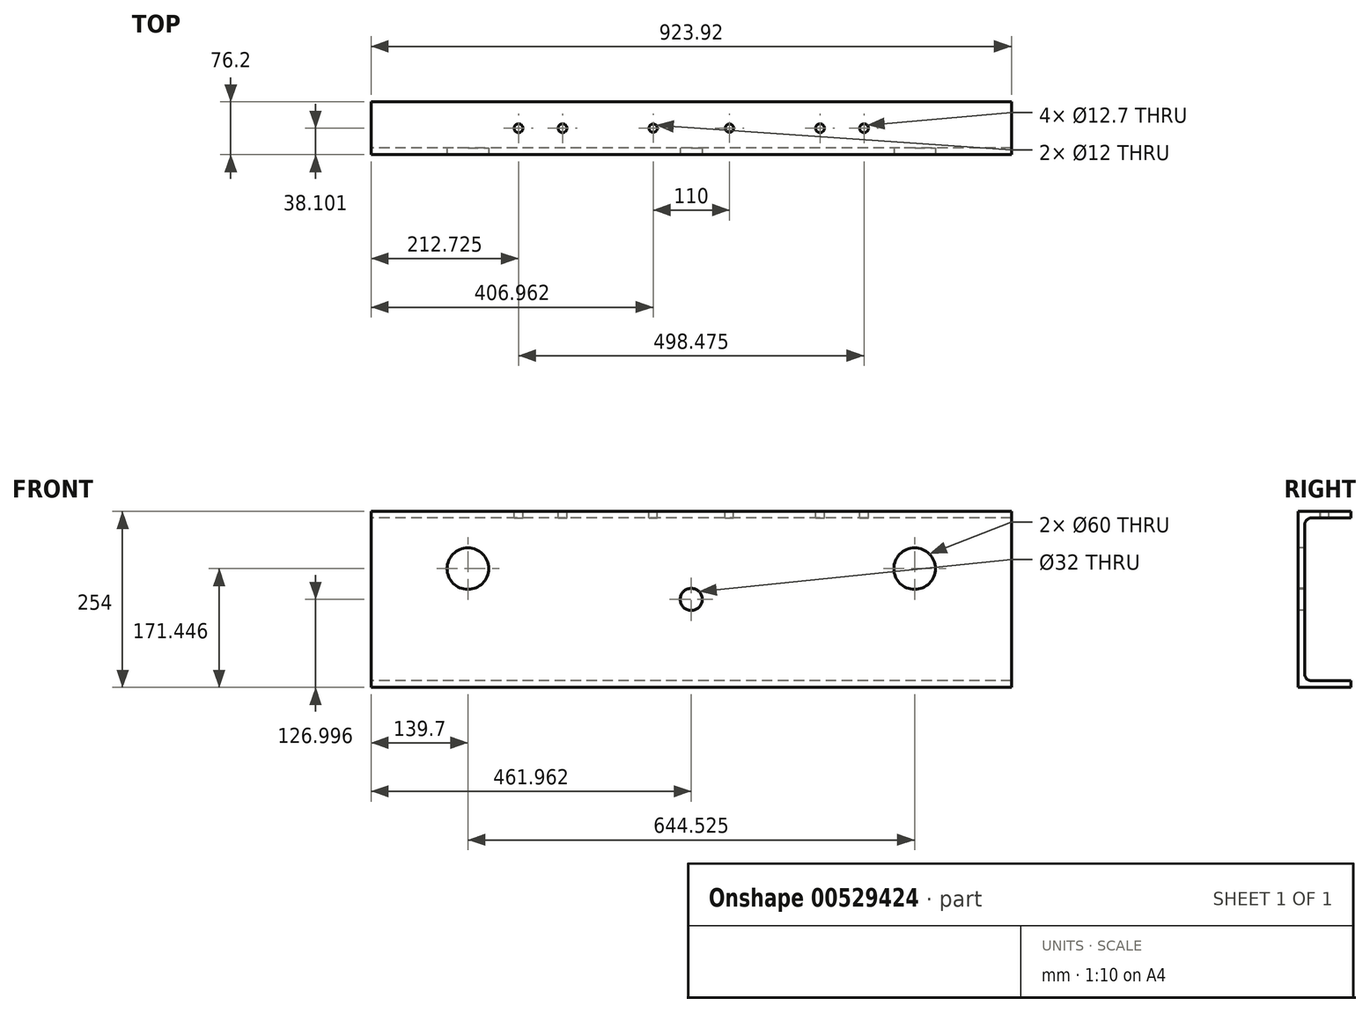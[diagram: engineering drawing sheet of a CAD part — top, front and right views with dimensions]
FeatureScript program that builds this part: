
annotation { "Feature Type Name" : "Feature", "Feature Type Description" : "" }
export const myFeature = defineFeature(function(context is Context, id is Id, definition is map)
    precondition{}
    {
        {
            var Q0;
            Q0=qCreatedBy(makeId("Right.planeOp"),FACE);
            var sketch = newSketch(context, id + "F0", { "sketchPlane" : qUnion([Q0])});
            skLineSegment(sketch, "E0", {"start": v(-26.57, -122.46) * mm, "end": v(-26.57, 131.54) * mm});
            skLineSegment(sketch, "E1", {"start": v(-26.57, 131.54) * mm, "end": v(49.63, 131.54) * mm});
            skLineSegment(sketch, "E2", {"start": v(49.63, 131.54) * mm, "end": v(49.63, 122.01) * mm});
            skLineSegment(sketch, "E3", {"start": v(49.63, 122.01) * mm, "end": v(-7.52, 122.01) * mm});
            skLineSegment(sketch, "E4", {"start": v(-17.04, 112.49) * mm, "end": v(-17.04, -103.41) * mm});
            skLineSegment(sketch, "E5", {"start": v(-7.52, -112.94) * mm, "end": v(49.63, -112.94) * mm});
            skLineSegment(sketch, "E6", {"start": v(49.63, -112.94) * mm, "end": v(49.63, -122.46) * mm});
            skLineSegment(sketch, "E7", {"start": v(49.63, -122.46) * mm, "end": v(-26.57, -122.46) * mm});
            skPoint(sketch, "E8.visualSharp", {"position": v(-17.04, 122.01) * mm});
            skArc(sketch, "E8.filletArc", {"start": v(-7.52, 122.01) * mm, "mid": v(-14.25, 119.22) * mm, "end": v(-17.04, 112.49) * mm});
            skPoint(sketch, "E9.visualSharp", {"position": v(-17.04, -112.94) * mm});
            skArc(sketch, "E9.filletArc", {"start": v(-17.04, -103.41) * mm, "mid": v(-14.25, -110.15) * mm, "end": v(-7.52, -112.94) * mm});
            skLineSegment(sketch, "E10", {"start": v(-26.57, -122.46) * mm, "end": v(-26.57, 4.54) * mm, "construction": true});
            skLineSegment(sketch, "E11", {"start": v(-26.57, 4.54) * mm, "end": v(-39.42, 4.54) * mm, "construction": true});
            skSolve(sketch);
        }
        {
            var Q0;
            Q0=makeQuery(id+"F0.imprint","IMPRINT",FACE,{"disambiguationData":[TD([[makeQuery(id+"F0.imprint","IMPRINT",EDGE,{"derivedFrom":sQuery(id+"F0.wireOp",EDGE,"E0")}),-1.0]])]});
            extrude(context, id + "F1", {"entities" : qUnion([Q0]), "depth" : 923.92 * mm, "offsetDistance" : 25 * mm});
        }
        {
            var Q0;
            Q0=makeQuery(id+"F1.opExtrude","SWEPT_FACE",FACE,{"disambiguationData":[OSD([sQuery(id+"F0.wireOp",EDGE,"E1")])]});
            var sketch = newSketch(context, id + "F2", { "sketchPlane" : qUnion([Q0])});
            skLineSegment(sketch, "E12.0", {"start": v(0, -26.57) * mm, "end": v(0, 49.63) * mm});
            skLineSegment(sketch, "E13.0", {"start": v(923.92, -26.57) * mm, "end": v(923.92, 49.63) * mm});
            skLineSegment(sketch, "E14", {"start": v(0, 11.53) * mm, "end": v(406.96, 11.53) * mm, "construction": true});
            skPoint(sketch, "E15", {"position": v(212.72, 11.53) * mm});
            skPoint(sketch, "E16", {"position": v(647.7, 11.53) * mm});
            skPoint(sketch, "E17", {"position": v(276.23, 11.53) * mm});
            skPoint(sketch, "E18", {"position": v(711.2, 11.53) * mm});
            skLineSegment(sketch, "E19", {"start": v(461.96, 11.53) * mm, "end": v(461.96, -11.52) * mm, "construction": true});
            skLineSegment(sketch, "E20", {"start": v(511.96, 11.53) * mm, "end": v(511.96, -10.3) * mm, "construction": true});
            skLineSegment(sketch, "E21", {"start": v(411.96, 11.53) * mm, "end": v(411.96, -9.07) * mm, "construction": true});
            skLineSegment(sketch, "E22", {"start": v(516.96, 11.53) * mm, "end": v(516.96, 26.4) * mm, "construction": true});
            skLineSegment(sketch, "E23", {"start": v(406.96, 11.53) * mm, "end": v(406.96, 26.4) * mm, "construction": true});
            skLineSegment(sketch, "E24", {"start": v(406.96, 11.53) * mm, "end": v(411.96, 11.53) * mm, "construction": true});
            skLineSegment(sketch, "E25", {"start": v(411.96, 11.53) * mm, "end": v(461.96, 11.53) * mm, "construction": true});
            skLineSegment(sketch, "E26", {"start": v(461.96, 11.53) * mm, "end": v(511.96, 11.53) * mm, "construction": true});
            skLineSegment(sketch, "E27", {"start": v(511.96, 11.53) * mm, "end": v(516.96, 11.53) * mm, "construction": true});
            skLineSegment(sketch, "E28", {"start": v(516.96, 11.53) * mm, "end": v(923.92, 11.53) * mm, "construction": true});
            skSolve(sketch);
        }
        {
            var Q0;
            Q0=sQuery(id+"F2.wireOp",VERTEX,"E15");
            var Q1;
            Q1=sQuery(id+"F2.wireOp",VERTEX,"E17");
            var Q2;
            Q2=sQuery(id+"F2.wireOp",VERTEX,"E16");
            var Q3;
            Q3=sQuery(id+"F2.wireOp",VERTEX,"E18");
            var Q4;
            Q4=makeQuery(id+"F1.opExtrude","SWEPT_BODY",BODY,{"disambiguationData":[OSD([sQuery(id+"F0.wireOp",EDGE,"E0"),sQuery(id+"F0.wireOp",EDGE,"E1"),sQuery(id+"F0.wireOp",EDGE,"E2"),sQuery(id+"F0.wireOp",EDGE,"E3"),sQuery(id+"F0.wireOp",EDGE,"E4"),sQuery(id+"F0.wireOp",EDGE,"E5"),sQuery(id+"F0.wireOp",EDGE,"E6"),sQuery(id+"F0.wireOp",EDGE,"E7"),sQuery(id+"F0.wireOp",EDGE,"E8.filletArc"),sQuery(id+"F0.wireOp",EDGE,"E9.filletArc")])]});
            hole(context, id + "F3", {"style" : HoleStyle.SIMPLE, "endStyle" : HoleEndStyle.BLIND, "holeDiameter" : 12.7 * mm, "holeDepth" : 30 * mm, "isTappedThrough" : true, "tappedDepth" : 12 * mm, "tapClearance" : 3, "locations" : qUnion([Q0, Q1, Q2, Q3]), "scope" : qUnion([Q4])});
        }
        {
            var Q0;
            Q0=makeQuery(id+"F1.opExtrude","SWEPT_FACE",FACE,{"disambiguationData":[OSD([sQuery(id+"F0.wireOp",EDGE,"E0")])]});
            var sketch = newSketch(context, id + "F4", { "sketchPlane" : qUnion([Q0])});
            skLineSegment(sketch, "E29.0", {"start": v(0, -122.46) * mm, "end": v(0, 131.54) * mm});
            skLineSegment(sketch, "E30.0", {"start": v(923.92, 131.54) * mm, "end": v(0, 131.54) * mm});
            skLineSegment(sketch, "E31.0", {"start": v(923.92, -122.46) * mm, "end": v(923.92, 131.54) * mm});
            skLineSegment(sketch, "E32.0", {"start": v(923.92, -122.46) * mm, "end": v(0, -122.46) * mm});
            skLineSegment(sketch, "E33", {"start": v(461.96, 131.54) * mm, "end": v(461.96, 4.54) * mm, "construction": true});
            skLineSegment(sketch, "E34", {"start": v(923.92, 48.99) * mm, "end": v(784.22, 48.99) * mm, "construction": true});
            skLineSegment(sketch, "E35.MirrorCS", {"start": v(0, 48.99) * mm, "end": v(139.7, 48.99) * mm, "construction": true});
            skLineSegment(sketch, "E36", {"start": v(461.96, 4.54) * mm, "end": v(461.96, -122.46) * mm, "construction": true});
            skSolve(sketch);
        }
        {
            var Q0;
            Q0=sQuery(id+"F4.wireOp",VERTEX,"E35.MirrorCS.end");
            var Q1;
            Q1=sQuery(id+"F4.wireOp",VERTEX,"E34.end");
            var Q2;
            Q2=makeQuery(id+"F1.opExtrude","SWEPT_BODY",BODY,{"disambiguationData":[OSD([sQuery(id+"F0.wireOp",EDGE,"E0"),sQuery(id+"F0.wireOp",EDGE,"E1"),sQuery(id+"F0.wireOp",EDGE,"E2"),sQuery(id+"F0.wireOp",EDGE,"E3"),sQuery(id+"F0.wireOp",EDGE,"E4"),sQuery(id+"F0.wireOp",EDGE,"E5"),sQuery(id+"F0.wireOp",EDGE,"E6"),sQuery(id+"F0.wireOp",EDGE,"E7"),sQuery(id+"F0.wireOp",EDGE,"E8.filletArc"),sQuery(id+"F0.wireOp",EDGE,"E9.filletArc")])]});
            hole(context, id + "F5", {"style" : HoleStyle.SIMPLE, "endStyle" : HoleEndStyle.BLIND, "holeDiameter" : 60 * mm, "holeDepth" : 30 * mm, "isTappedThrough" : true, "tappedDepth" : 12 * mm, "tapClearance" : 3, "locations" : qUnion([Q0, Q1]), "scope" : qUnion([Q2])});
        }
        {
            var Q0;
            Q0=sQuery(id+"F4.wireOp",VERTEX,"E36.start");
            var Q1;
            Q1=makeQuery(id+"F1.opExtrude","SWEPT_BODY",BODY,{"disambiguationData":[OSD([sQuery(id+"F0.wireOp",EDGE,"E0"),sQuery(id+"F0.wireOp",EDGE,"E1"),sQuery(id+"F0.wireOp",EDGE,"E2"),sQuery(id+"F0.wireOp",EDGE,"E3"),sQuery(id+"F0.wireOp",EDGE,"E4"),sQuery(id+"F0.wireOp",EDGE,"E5"),sQuery(id+"F0.wireOp",EDGE,"E6"),sQuery(id+"F0.wireOp",EDGE,"E7"),sQuery(id+"F0.wireOp",EDGE,"E8.filletArc"),sQuery(id+"F0.wireOp",EDGE,"E9.filletArc")])]});
            hole(context, id + "F6", {"style" : HoleStyle.SIMPLE, "endStyle" : HoleEndStyle.BLIND, "holeDiameter" : 32 * mm, "holeDepth" : 30 * mm, "isTappedThrough" : true, "tappedDepth" : 12 * mm, "tapClearance" : 3, "locations" : qUnion([Q0]), "scope" : qUnion([Q1])});
        }
        {
            var Q0;
            Q0=sQuery(id+"F2.wireOp",VERTEX,"E14.end");
            var Q1;
            Q1=sQuery(id+"F2.wireOp",VERTEX,"E27.end");
            var Q2;
            Q2=makeQuery(id+"F1.opExtrude","SWEPT_BODY",BODY,{"disambiguationData":[OSD([sQuery(id+"F0.wireOp",EDGE,"E0"),sQuery(id+"F0.wireOp",EDGE,"E1"),sQuery(id+"F0.wireOp",EDGE,"E2"),sQuery(id+"F0.wireOp",EDGE,"E3"),sQuery(id+"F0.wireOp",EDGE,"E4"),sQuery(id+"F0.wireOp",EDGE,"E5"),sQuery(id+"F0.wireOp",EDGE,"E6"),sQuery(id+"F0.wireOp",EDGE,"E7"),sQuery(id+"F0.wireOp",EDGE,"E8.filletArc"),sQuery(id+"F0.wireOp",EDGE,"E9.filletArc")])]});
            hole(context, id + "F7", {"style" : HoleStyle.SIMPLE, "endStyle" : HoleEndStyle.BLIND, "holeDiameter" : 12 * mm, "holeDepth" : 30 * mm, "isTappedThrough" : true, "tappedDepth" : 12 * mm, "tapClearance" : 3, "locations" : qUnion([Q0, Q1]), "scope" : qUnion([Q2])});
        }
    });
